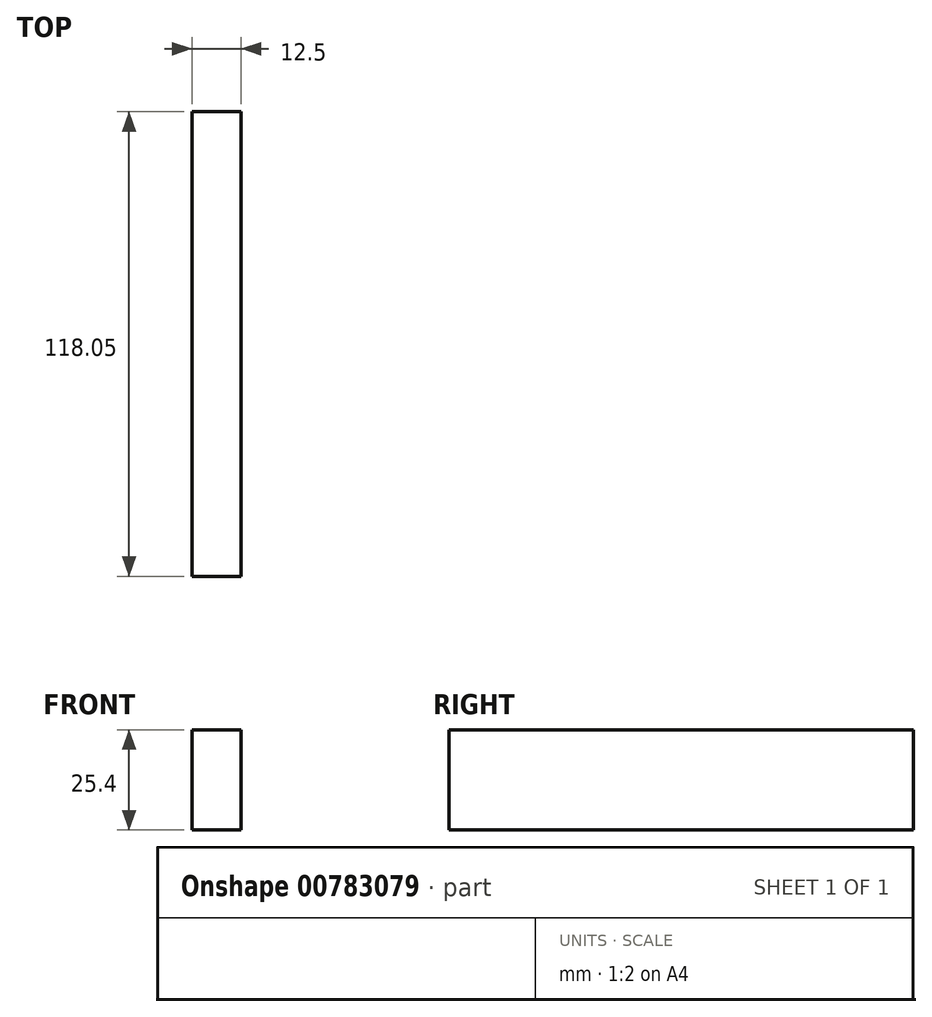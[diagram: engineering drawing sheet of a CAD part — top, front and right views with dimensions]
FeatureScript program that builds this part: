
annotation { "Feature Type Name" : "Feature", "Feature Type Description" : "" }
export const myFeature = defineFeature(function(context is Context, id is Id, definition is map)
    precondition{}
    {
        {
            var Q0;
            Q0=qCreatedBy(makeId("Top.planeOp"),FACE);
            var sketch = newSketch(context, id + "F0", { "sketchPlane" : qUnion([Q0])});
            skLineSegment(sketch, "E0.bottom", {"start": v(0, 64.03) * mm, "end": v(-12.5, 64.03) * mm});
            skLineSegment(sketch, "E0.top", {"start": v(0, -54.02) * mm, "end": v(-12.5, -54.02) * mm});
            skLineSegment(sketch, "E0.left", {"start": v(0, 64.03) * mm, "end": v(0, -54.02) * mm});
            skLineSegment(sketch, "E0.right", {"start": v(-12.5, 64.03) * mm, "end": v(-12.5, -54.02) * mm});
            skSolve(sketch);
        }
        {
            var Q0;
            Q0=sQuery(id+"F0.wireOp",EDGE,"E0.right");
            var Q1;
            Q1=sQuery(id+"F0.wireOp",EDGE,"E0.left");
            var Q2;
            Q2=sQuery(id+"F0.wireOp",EDGE,"E0.bottom");
            var Q3;
            Q3=sQuery(id+"F0.wireOp",EDGE,"E0.top");
            extrude(context, id + "F1", {"bodyType" : ToolBodyType.SURFACE, "surfaceEntities" : qUnion([Q0, Q1, Q2, Q3]), "depth" : 25.4 * mm, "offsetDistance" : 25.4 * mm});
        }
    });
